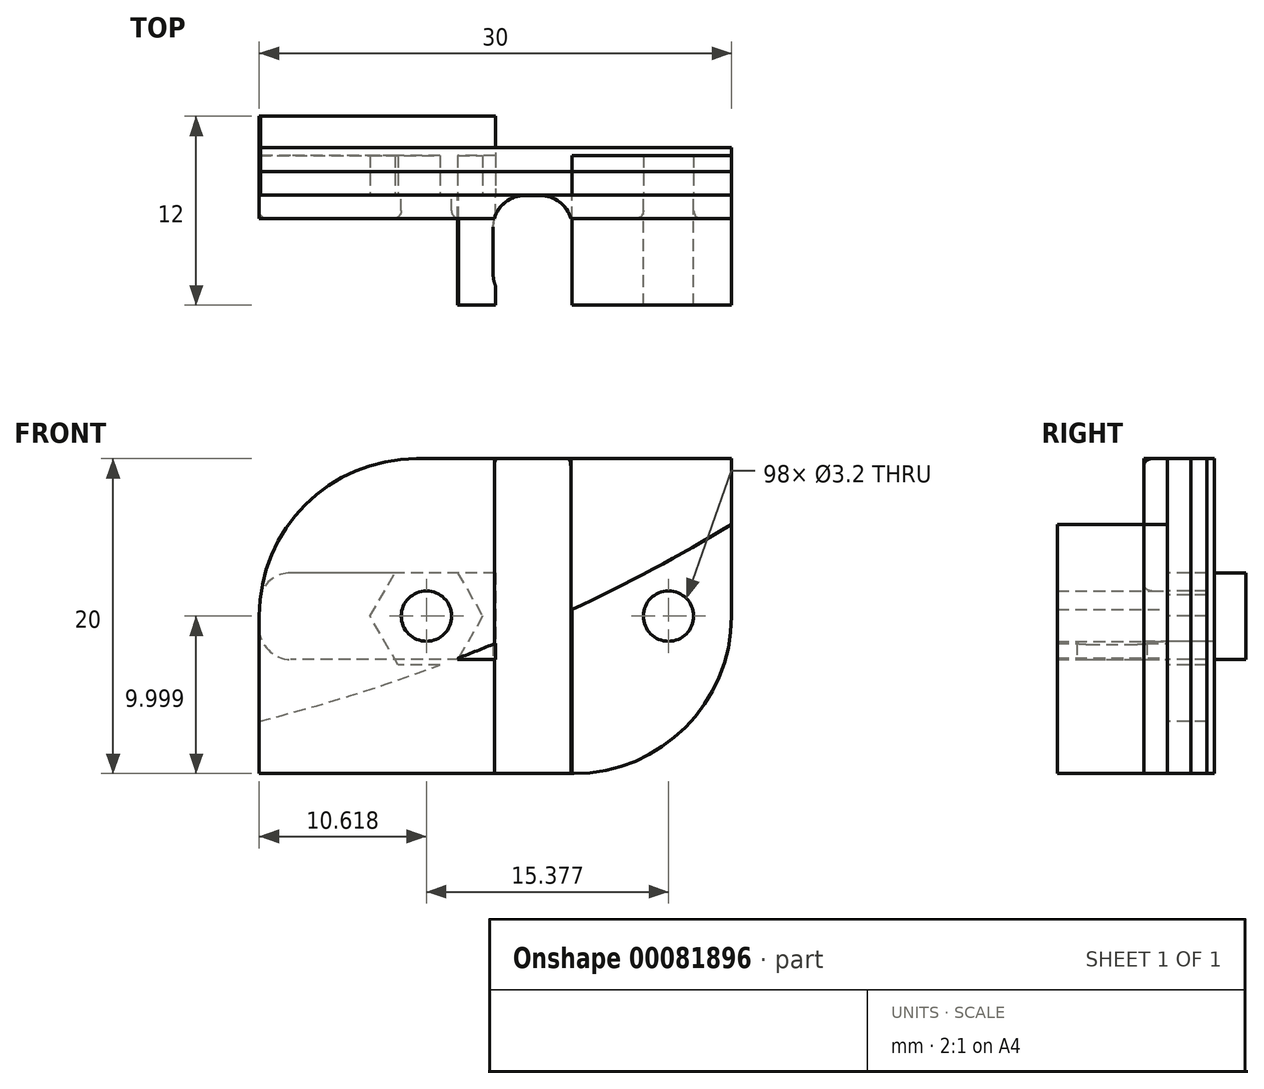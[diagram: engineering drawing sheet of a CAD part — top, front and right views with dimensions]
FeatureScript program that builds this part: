
annotation { "Feature Type Name" : "Feature", "Feature Type Description" : "" }
export const myFeature = defineFeature(function(context is Context, id is Id, definition is map)
    precondition{}
    {
        {
            var Q0;
            Q0=qCreatedBy(makeId("Front.planeOp"),FACE);
            var sketch = newSketch(context, id + "F0", { "sketchPlane" : qUnion([Q0])});
            skLineSegment(sketch, "E0", {"start": v(-99.36, 18.95) * mm, "end": v(51.56, 18.95) * mm, "construction": true});
            skCircle(sketch, "E1", {"center": v(-82.01, 118.95) * mm, "radius": 110 * mm});
            skLineSegment(sketch, "E2.bottom", {"start": v(-45.16, 28.95) * mm, "end": v(-25.16, 28.95) * mm});
            skLineSegment(sketch, "E2.top", {"start": v(-55.16, 8.95) * mm, "end": v(-35.16, 8.95) * mm});
            skLineSegment(sketch, "E2.left", {"start": v(-55.16, 18.95) * mm, "end": v(-55.16, 8.95) * mm});
            skLineSegment(sketch, "E2.right", {"start": v(-25.16, 28.95) * mm, "end": v(-25.16, 18.95) * mm});
            skCircle(sketch, "E3", {"center": v(-29.16, 18.95) * mm, "radius": 1.6 * mm});
            skCircle(sketch, "E4", {"center": v(-44.54, 18.95) * mm, "radius": 5 * mm, "construction": true});
            skPoint(sketch, "E5.visualSharp", {"position": v(-55.16, 28.95) * mm});
            skArc(sketch, "E5.filletArc", {"start": v(-45.16, 28.95) * mm, "mid": v(-52.24, 26.02) * mm, "end": v(-55.16, 18.95) * mm});
            skPoint(sketch, "E6.visualSharp", {"position": v(-25.16, 8.95) * mm});
            skArc(sketch, "E6.filletArc", {"start": v(-35.16, 8.95) * mm, "mid": v(-28.1, 11.88) * mm, "end": v(-25.16, 18.95) * mm});
            skLineSegment(sketch, "E7.bottom", {"start": v(-40.16, 21.7) * mm, "end": v(-53.16, 21.7) * mm});
            skLineSegment(sketch, "E7.top", {"start": v(-40.16, 16.2) * mm, "end": v(-53.16, 16.2) * mm});
            skLineSegment(sketch, "E7.left", {"start": v(-40.16, 21.7) * mm, "end": v(-40.16, 16.2) * mm});
            skLineSegment(sketch, "E7.right", {"start": v(-55.16, 19.7) * mm, "end": v(-55.16, 18.2) * mm});
            skPoint(sketch, "E7.middle", {"position": v(-47.66, 18.95) * mm});
            skCircle(sketch, "E8", {"center": v(-44.54, 18.95) * mm, "radius": 1.6 * mm});
            skLineSegment(sketch, "E9.bottom", {"start": v(-25.16, 28.95) * mm, "end": v(-35.3, 28.95) * mm});
            skLineSegment(sketch, "E9.top", {"start": v(-35.16, 8.95) * mm, "end": v(-35.3, 8.95) * mm});
            skLineSegment(sketch, "E9.right", {"start": v(-35.3, 28.95) * mm, "end": v(-35.3, 8.95) * mm});
            skPoint(sketch, "E10.visualSharp", {"position": v(-55.16, 21.7) * mm});
            skArc(sketch, "E10.filletArc", {"start": v(-53.16, 21.7) * mm, "mid": v(-54.58, 21.11) * mm, "end": v(-55.16, 19.7) * mm});
            skPoint(sketch, "E11.visualSharp", {"position": v(-55.16, 16.2) * mm});
            skArc(sketch, "E11.filletArc", {"start": v(-55.16, 18.2) * mm, "mid": v(-54.58, 16.78) * mm, "end": v(-53.16, 16.2) * mm});
            skCircle(sketch, "E12.cCircle", {"center": v(-44.54, 18.95) * mm, "radius": 3.1 * mm, "construction": true});
            skLineSegment(sketch, "E12.0", {"start": v(-42.75, 22.05) * mm, "end": v(-40.96, 18.95) * mm});
            skLineSegment(sketch, "E12.1", {"start": v(-40.96, 18.95) * mm, "end": v(-42.75, 15.85) * mm});
            skLineSegment(sketch, "E12.2", {"start": v(-42.75, 15.85) * mm, "end": v(-46.33, 15.85) * mm});
            skLineSegment(sketch, "E12.3", {"start": v(-46.33, 15.85) * mm, "end": v(-48.12, 18.95) * mm});
            skLineSegment(sketch, "E12.4", {"start": v(-48.12, 18.95) * mm, "end": v(-46.33, 22.05) * mm});
            skLineSegment(sketch, "E12.5", {"start": v(-46.33, 22.05) * mm, "end": v(-42.75, 22.05) * mm});
            skPoint(sketch, "E12.0.midPoint", {"position": v(-41.86, 20.5) * mm});
            skSolve(sketch);
        }
        {
            var Q0;
            Q0=makeQuery(id+"F0.imprint","IMPRINT",FACE,{"disambiguationData":[TD([[makeQuery(id+"F0.imprint","IMPRINT",EDGE,{"derivedFrom":sQuery(id+"F0.wireOp",EDGE,"E3")}),-1.0]])]});
            var Q1;
            {var subQ5=sQuery(id+"F0.wireOp",EDGE,"E9.bottom");Q1=makeQuery(id+"F0.imprint","IMPRINT",FACE,{"disambiguationData":[TD([[makeQuery(id+"F0.imprint","IMPRINT",EDGE,{"derivedFrom":subQ5}),1.0]])]});}
            var Q2;
            {var subQ12=sQuery(id+"F0.wireOp",EDGE,"E2.bottom");Q2=makeQuery(id+"F0.imprint","IMPRINT",FACE,{"disambiguationData":[TD([[makeQuery(id+"F0.imprint","IMPRINT",EDGE,{"derivedFrom":subQ12}),-1.0]])]});}
            var Q3;
            {var subQ1=sQuery(id+"F0.wireOp",EDGE,"E2.top");Q3=makeQuery(id+"F0.imprint","IMPRINT",FACE,{"disambiguationData":[TD([[makeQuery(id+"F0.imprint","IMPRINT",EDGE,{"derivedFrom":subQ1}),1.0]])]});}
            var Q4;
            {var subQ3=sQuery(id+"F0.wireOp",EDGE,"E7.bottom");var subQ5=sQuery(id+"F0.wireOp",EDGE,"E4");var subQ7=makeQuery(id+"F0.imprint","INTERSECT",VERTEX,{"disambiguationData":[OD(0.0)],"derivedFrom":[subQ5,subQ3]});Q4=makeQuery(id+"F0.imprint","IMPRINT",FACE,{"disambiguationData":[TD([[makeQuery(id+"F0.imprint","IMPRINT",EDGE,{"disambiguationData":[TD([[subQ7,-1.0]])],"derivedFrom":subQ5}),1.0]])]});}
            var Q5;
            {var subQ12=sQuery(id+"F0.wireOp",EDGE,"8888e60d-31c4-49a8-b3cd-6678c98749ca.5");Q5=makeQuery(id+"F0.imprint","IMPRINT",FACE,{"disambiguationData":[TD([[makeQuery(id+"F0.imprint","IMPRINT",EDGE,{"derivedFrom":subQ12}),1.0]])]});}
            var Q6;
            {var subQ0=sQuery(id+"F0.wireOp",EDGE,"E7.left");var subQ1=sQuery(id+"F0.wireOp",EDGE,"E1");var subQ2=makeQuery(id+"F0.imprint","INTERSECT",VERTEX,{"derivedFrom":[subQ1,subQ0]});Q6=makeQuery(id+"F0.imprint","IMPRINT",FACE,{"disambiguationData":[TD([[makeQuery(id+"F0.imprint","IMPRINT",EDGE,{"disambiguationData":[TD([[subQ2,-1.0]])],"derivedFrom":subQ1}),1.0]])]});}
            var Q7;
            {var subQ0=sQuery(id+"F0.wireOp",EDGE,"E4");var subQ1=sQuery(id+"F0.wireOp",EDGE,"E1");var subQ2=makeQuery(id+"F0.imprint","INTERSECT",VERTEX,{"disambiguationData":[OD(0.0)],"derivedFrom":[subQ1,subQ0]});Q7=makeQuery(id+"F0.imprint","IMPRINT",FACE,{"disambiguationData":[TD([[makeQuery(id+"F0.imprint","IMPRINT",EDGE,{"disambiguationData":[TD([[subQ2,-1.0]])],"derivedFrom":subQ1}),-1.0]])]});}
            var Q8;
            {var subQ0=sQuery(id+"F0.wireOp",EDGE,"E7.top");var subQ1=sQuery(id+"F0.wireOp",EDGE,"E1");var subQ2=makeQuery(id+"F0.imprint","INTERSECT",VERTEX,{"derivedFrom":[subQ1,subQ0]});Q8=makeQuery(id+"F0.imprint","IMPRINT",FACE,{"disambiguationData":[TD([[makeQuery(id+"F0.imprint","IMPRINT",EDGE,{"disambiguationData":[TD([[subQ2,-1.0]])],"derivedFrom":subQ1}),-1.0]])]});}
            var Q9;
            {var subQ1=sQuery(id+"F0.wireOp",EDGE,"E4");var subQ5=sQuery(id+"F0.wireOp",EDGE,"E1");var subQ9=makeQuery(id+"F0.imprint","INTERSECT",VERTEX,{"disambiguationData":[OD(0.0)],"derivedFrom":[subQ5,subQ1]});Q9=makeQuery(id+"F0.imprint","IMPRINT",FACE,{"disambiguationData":[TD([[makeQuery(id+"F0.imprint","IMPRINT",EDGE,{"disambiguationData":[TD([[subQ9,-1.0]])],"derivedFrom":subQ5}),1.0]])]});}
            var Q10;
            Q10=makeQuery(id+"F0.imprint","IMPRINT",FACE,{"disambiguationData":[TD([[makeQuery(id+"F0.imprint","IMPRINT",EDGE,{"derivedFrom":sQuery(id+"F0.wireOp",EDGE,"E8")}),-1.0]])]});
            var Q11;
            {var subQ0=sQuery(id+"F0.wireOp",EDGE,"8888e60d-31c4-49a8-b3cd-6678c98749ca.4");var subQ1=sQuery(id+"F0.wireOp",EDGE,"E7.bottom");var subQ2=makeQuery(id+"F0.imprint","INTERSECT",VERTEX,{"derivedFrom":[subQ1,subQ0]});Q11=makeQuery(id+"F0.imprint","IMPRINT",FACE,{"disambiguationData":[TD([[makeQuery(id+"F0.imprint","IMPRINT",EDGE,{"disambiguationData":[TD([[subQ2,-1.0]])],"derivedFrom":subQ1}),-1.0]])]});}
            var Q12;
            {var subQ5=sQuery(id+"F0.wireOp",EDGE,"8888e60d-31c4-49a8-b3cd-6678c98749ca.2");Q12=makeQuery(id+"F0.imprint","IMPRINT",FACE,{"disambiguationData":[TD([[makeQuery(id+"F0.imprint","IMPRINT",EDGE,{"derivedFrom":subQ5}),1.0]])]});}
            var Q13;
            {var subQ0=sQuery(id+"F0.wireOp",EDGE,"E11.filletArc");Q13=makeQuery(id+"F0.imprint","IMPRINT",FACE,{"disambiguationData":[TD([[makeQuery(id+"F0.imprint","IMPRINT",EDGE,{"derivedFrom":subQ0}),1.0]])]});}
            var Q14;
            {var subQ5=sQuery(id+"F0.wireOp",EDGE,"E11.filletArc");Q14=makeQuery(id+"F0.imprint","IMPRINT",FACE,{"disambiguationData":[TD([[makeQuery(id+"F0.imprint","IMPRINT",EDGE,{"derivedFrom":subQ5}),-1.0]])]});}
            var Q15;
            {var subQ0=sQuery(id+"F0.wireOp",EDGE,"8888e60d-31c4-49a8-b3cd-6678c98749ca.0");var subQ1=sQuery(id+"F0.wireOp",EDGE,"E7.top");var subQ2=makeQuery(id+"F0.imprint","INTERSECT",VERTEX,{"derivedFrom":[subQ1,subQ0]});Q15=makeQuery(id+"F0.imprint","IMPRINT",FACE,{"disambiguationData":[TD([[makeQuery(id+"F0.imprint","IMPRINT",EDGE,{"disambiguationData":[TD([[subQ2,-1.0]])],"derivedFrom":subQ1}),1.0]])]});}
            var Q16;
            {var subQ0=sQuery(id+"F0.wireOp",EDGE,"E7.left");var subQ1=sQuery(id+"F0.wireOp",EDGE,"E1");var subQ2=makeQuery(id+"F0.imprint","INTERSECT",VERTEX,{"derivedFrom":[subQ1,subQ0]});Q16=makeQuery(id+"F0.imprint","IMPRINT",FACE,{"disambiguationData":[TD([[makeQuery(id+"F0.imprint","IMPRINT",EDGE,{"disambiguationData":[TD([[subQ2,-1.0]])],"derivedFrom":subQ1}),-1.0]])]});}
            var Q17;
            {var subQ0=sQuery(id+"F0.wireOp",EDGE,"E7.top");var subQ1=sQuery(id+"F0.wireOp",EDGE,"E4");var subQ2=makeQuery(id+"F0.imprint","INTERSECT",VERTEX,{"disambiguationData":[OD(1.0)],"derivedFrom":[subQ1,subQ0]});Q17=makeQuery(id+"F0.imprint","IMPRINT",FACE,{"disambiguationData":[TD([[makeQuery(id+"F0.imprint","IMPRINT",EDGE,{"disambiguationData":[TD([[subQ2,-1.0]])],"derivedFrom":subQ1}),-1.0]])]});}
            var Q18;
            {var subQ0=sQuery(id+"F0.wireOp",EDGE,"E7.bottom");var subQ1=sQuery(id+"F0.wireOp",EDGE,"E4");var subQ2=makeQuery(id+"F0.imprint","INTERSECT",VERTEX,{"disambiguationData":[OD(0.0)],"derivedFrom":[subQ1,subQ0]});Q18=makeQuery(id+"F0.imprint","IMPRINT",FACE,{"disambiguationData":[TD([[makeQuery(id+"F0.imprint","IMPRINT",EDGE,{"disambiguationData":[TD([[subQ2,1.0]])],"derivedFrom":subQ1}),-1.0]])]});}
            var Q19;
            {var subQ5=sQuery(id+"F0.wireOp",EDGE,"E12.5");Q19=makeQuery(id+"F0.imprint","IMPRINT",FACE,{"disambiguationData":[TD([[makeQuery(id+"F0.imprint","IMPRINT",EDGE,{"derivedFrom":subQ5}),-1.0]])]});}
            var Q20;
            {var subQ0=sQuery(id+"F0.wireOp",EDGE,"E12.1");var subQ5=sQuery(id+"F0.wireOp",EDGE,"E1");var subQ6=makeQuery(id+"F0.imprint","INTERSECT",VERTEX,{"derivedFrom":[subQ5,subQ0]});Q20=makeQuery(id+"F0.imprint","IMPRINT",FACE,{"disambiguationData":[TD([[makeQuery(id+"F0.imprint","IMPRINT",EDGE,{"disambiguationData":[TD([[subQ6,-1.0]])],"derivedFrom":subQ5}),1.0]])]});}
            var Q21;
            {var subQ0=sQuery(id+"F0.wireOp",EDGE,"E12.1");var subQ1=sQuery(id+"F0.wireOp",EDGE,"E1");var subQ2=makeQuery(id+"F0.imprint","INTERSECT",VERTEX,{"derivedFrom":[subQ1,subQ0]});Q21=makeQuery(id+"F0.imprint","IMPRINT",FACE,{"disambiguationData":[TD([[makeQuery(id+"F0.imprint","IMPRINT",EDGE,{"disambiguationData":[TD([[subQ2,-1.0]])],"derivedFrom":subQ1}),-1.0]])]});}
            extrude(context, id + "F1", {"entities" : qUnion([Q0, Q1, Q2, Q3, Q4, Q5, Q6, Q7, Q8, Q9, Q10, Q11, Q12, Q13, Q14, Q15, Q16, Q17, Q18, Q19, Q20, Q21]), "depth" : 1.5 * mm});
        }
        {
            var Q0;
            {var subQ5=sQuery(id+"F0.wireOp",EDGE,"E9.bottom");Q0=makeQuery(id+"F0.imprint","IMPRINT",FACE,{"disambiguationData":[TD([[makeQuery(id+"F0.imprint","IMPRINT",EDGE,{"derivedFrom":subQ5}),1.0]])]});}
            var Q1;
            Q1=makeQuery(id+"F0.imprint","IMPRINT",FACE,{"disambiguationData":[TD([[makeQuery(id+"F0.imprint","IMPRINT",EDGE,{"derivedFrom":sQuery(id+"F0.wireOp",EDGE,"E3")}),-1.0]])]});
            var Q2;
            {var subQ1=sQuery(id+"F0.wireOp",EDGE,"E2.top");Q2=makeQuery(id+"F0.imprint","IMPRINT",FACE,{"disambiguationData":[TD([[makeQuery(id+"F0.imprint","IMPRINT",EDGE,{"derivedFrom":subQ1}),1.0]])]});}
            var Q3;
            {var subQ10=sQuery(id+"F0.wireOp",EDGE,"E2.bottom");Q3=makeQuery(id+"F0.imprint","IMPRINT",FACE,{"disambiguationData":[TD([[makeQuery(id+"F0.imprint","IMPRINT",EDGE,{"derivedFrom":subQ10}),-1.0]])]});}
            var Q4;
            {var subQ0=sQuery(id+"F0.wireOp",EDGE,"E11.filletArc");Q4=makeQuery(id+"F0.imprint","IMPRINT",FACE,{"disambiguationData":[TD([[makeQuery(id+"F0.imprint","IMPRINT",EDGE,{"derivedFrom":subQ0}),-1.0]])]});}
            var Q5;
            {var subQ9=sQuery(id+"F0.wireOp",EDGE,"E11.filletArc");Q5=makeQuery(id+"F0.imprint","IMPRINT",FACE,{"disambiguationData":[TD([[makeQuery(id+"F0.imprint","IMPRINT",EDGE,{"derivedFrom":subQ9}),1.0]])]});}
            var Q6;
            {var subQ0=sQuery(id+"F0.wireOp",EDGE,"E7.bottom");var subQ1=sQuery(id+"F0.wireOp",EDGE,"E4");var subQ2=makeQuery(id+"F0.imprint","INTERSECT",VERTEX,{"disambiguationData":[OD(0.0)],"derivedFrom":[subQ1,subQ0]});Q6=makeQuery(id+"F0.imprint","IMPRINT",FACE,{"disambiguationData":[TD([[makeQuery(id+"F0.imprint","IMPRINT",EDGE,{"disambiguationData":[TD([[subQ2,1.0]])],"derivedFrom":subQ1}),-1.0]])]});}
            var Q7;
            {var subQ0=sQuery(id+"F0.wireOp",EDGE,"E7.top");var subQ1=sQuery(id+"F0.wireOp",EDGE,"E4");var subQ2=makeQuery(id+"F0.imprint","INTERSECT",VERTEX,{"disambiguationData":[OD(1.0)],"derivedFrom":[subQ1,subQ0]});Q7=makeQuery(id+"F0.imprint","IMPRINT",FACE,{"disambiguationData":[TD([[makeQuery(id+"F0.imprint","IMPRINT",EDGE,{"disambiguationData":[TD([[subQ2,-1.0]])],"derivedFrom":subQ1}),-1.0]])]});}
            var Q8;
            {var subQ0=sQuery(id+"F0.wireOp",EDGE,"E12.1");var subQ5=sQuery(id+"F0.wireOp",EDGE,"E1");var subQ6=makeQuery(id+"F0.imprint","INTERSECT",VERTEX,{"derivedFrom":[subQ5,subQ0]});Q8=makeQuery(id+"F0.imprint","IMPRINT",FACE,{"disambiguationData":[TD([[makeQuery(id+"F0.imprint","IMPRINT",EDGE,{"disambiguationData":[TD([[subQ6,-1.0]])],"derivedFrom":subQ5}),1.0]])]});}
            var Q9;
            {var subQ0=sQuery(id+"F0.wireOp",EDGE,"E12.1");var subQ1=sQuery(id+"F0.wireOp",EDGE,"E1");var subQ2=makeQuery(id+"F0.imprint","INTERSECT",VERTEX,{"derivedFrom":[subQ1,subQ0]});Q9=makeQuery(id+"F0.imprint","IMPRINT",FACE,{"disambiguationData":[TD([[makeQuery(id+"F0.imprint","IMPRINT",EDGE,{"disambiguationData":[TD([[subQ2,-1.0]])],"derivedFrom":subQ1}),-1.0]])]});}
            extrude(context, id + "F2", {"entities" : qUnion([Q0, Q1, Q2, Q3, Q4, Q5, Q6, Q7, Q8, Q9]), "oppositeDirection" : true, "depth" : 2.5 * mm});
        }
        {
            var Q0;
            {var subQ1=sQuery(id+"F0.wireOp",EDGE,"E2.top");Q0=makeQuery(id+"F0.imprint","IMPRINT",FACE,{"disambiguationData":[TD([[makeQuery(id+"F0.imprint","IMPRINT",EDGE,{"derivedFrom":subQ1}),1.0]])]});}
            var Q1;
            Q1=makeQuery(id+"F0.imprint","IMPRINT",FACE,{"disambiguationData":[TD([[makeQuery(id+"F0.imprint","IMPRINT",EDGE,{"derivedFrom":sQuery(id+"F0.wireOp",EDGE,"E3")}),-1.0]])]});
            var Q2;
            {var subQ0=sQuery(id+"F0.wireOp",EDGE,"E7.top");var subQ1=sQuery(id+"F0.wireOp",EDGE,"E4");var subQ2=makeQuery(id+"F0.imprint","INTERSECT",VERTEX,{"disambiguationData":[OD(1.0)],"derivedFrom":[subQ1,subQ0]});Q2=makeQuery(id+"F0.imprint","IMPRINT",FACE,{"disambiguationData":[TD([[makeQuery(id+"F0.imprint","IMPRINT",EDGE,{"disambiguationData":[TD([[subQ2,-1.0]])],"derivedFrom":subQ1}),-1.0]])]});}
            var Q3;
            {var subQ0=sQuery(id+"F0.wireOp",EDGE,"E12.1");var subQ1=sQuery(id+"F0.wireOp",EDGE,"E1");var subQ2=makeQuery(id+"F0.imprint","INTERSECT",VERTEX,{"derivedFrom":[subQ1,subQ0]});Q3=makeQuery(id+"F0.imprint","IMPRINT",FACE,{"disambiguationData":[TD([[makeQuery(id+"F0.imprint","IMPRINT",EDGE,{"disambiguationData":[TD([[subQ2,-1.0]])],"derivedFrom":subQ1}),-1.0]])]});}
            extrude(context, id + "F3", {"entities" : qUnion([Q0, Q1, Q2, Q3]), "depth" : 7 * mm});
        }
        {
            var Q0;
            {var subQ9=sQuery(id+"F0.wireOp",EDGE,"E11.filletArc");Q0=makeQuery(id+"F0.imprint","IMPRINT",FACE,{"disambiguationData":[TD([[makeQuery(id+"F0.imprint","IMPRINT",EDGE,{"derivedFrom":subQ9}),1.0]])]});}
            var Q1;
            Q1=makeQuery(id+"F0.imprint","IMPRINT",FACE,{"disambiguationData":[TD([[makeQuery(id+"F0.imprint","IMPRINT",EDGE,{"derivedFrom":sQuery(id+"F0.wireOp",EDGE,"E8")}),-1.0]])]});
            var Q2;
            {var subQ0=sQuery(id+"F0.wireOp",EDGE,"E7.top");var subQ1=sQuery(id+"F0.wireOp",EDGE,"E1");var subQ2=makeQuery(id+"F0.imprint","INTERSECT",VERTEX,{"derivedFrom":[subQ1,subQ0]});Q2=makeQuery(id+"F0.imprint","IMPRINT",FACE,{"disambiguationData":[TD([[makeQuery(id+"F0.imprint","IMPRINT",EDGE,{"disambiguationData":[TD([[subQ2,-1.0]])],"derivedFrom":subQ1}),-1.0]])]});}
            var Q3;
            Q3=makeQuery(id+"F0.imprint","IMPRINT",FACE,{"disambiguationData":[TD([[makeQuery(id+"F0.imprint","IMPRINT",EDGE,{"derivedFrom":sQuery(id+"F0.wireOp",EDGE,"E8")}),1.0]])]});
            var Q4;
            {var subQ0=sQuery(id+"F0.wireOp",EDGE,"E12.1");var subQ5=sQuery(id+"F0.wireOp",EDGE,"E1");var subQ6=makeQuery(id+"F0.imprint","INTERSECT",VERTEX,{"derivedFrom":[subQ5,subQ0]});Q4=makeQuery(id+"F0.imprint","IMPRINT",FACE,{"disambiguationData":[TD([[makeQuery(id+"F0.imprint","IMPRINT",EDGE,{"disambiguationData":[TD([[subQ6,-1.0]])],"derivedFrom":subQ5}),1.0]])]});}
            var Q5;
            {var subQ0=sQuery(id+"F0.wireOp",EDGE,"E12.1");var subQ1=sQuery(id+"F0.wireOp",EDGE,"E1");var subQ2=makeQuery(id+"F0.imprint","INTERSECT",VERTEX,{"derivedFrom":[subQ1,subQ0]});Q5=makeQuery(id+"F0.imprint","IMPRINT",FACE,{"disambiguationData":[TD([[makeQuery(id+"F0.imprint","IMPRINT",EDGE,{"disambiguationData":[TD([[subQ2,-1.0]])],"derivedFrom":subQ1}),-1.0]])]});}
            extrude(context, id + "F4", {"entities" : qUnion([Q0, Q1, Q2, Q3, Q4, Q5]), "oppositeDirection" : true, "depth" : 5 * mm});
        }
        {
            var Q0;
            {var subQ10=sQuery(id+"F0.wireOp",EDGE,"E2.bottom");Q0=makeQuery(id+"F0.imprint","IMPRINT",FACE,{"disambiguationData":[TD([[makeQuery(id+"F0.imprint","IMPRINT",EDGE,{"derivedFrom":subQ10}),-1.0]])]});}
            var Q1;
            {var subQ0=sQuery(id+"F0.wireOp",EDGE,"E7.bottom");var subQ1=sQuery(id+"F0.wireOp",EDGE,"E4");var subQ2=makeQuery(id+"F0.imprint","INTERSECT",VERTEX,{"disambiguationData":[OD(0.0)],"derivedFrom":[subQ1,subQ0]});Q1=makeQuery(id+"F0.imprint","IMPRINT",FACE,{"disambiguationData":[TD([[makeQuery(id+"F0.imprint","IMPRINT",EDGE,{"disambiguationData":[TD([[subQ2,-1.0]])],"derivedFrom":subQ1}),1.0]])]});}
            var Q2;
            {var subQ9=sQuery(id+"F0.wireOp",EDGE,"E11.filletArc");Q2=makeQuery(id+"F0.imprint","IMPRINT",FACE,{"disambiguationData":[TD([[makeQuery(id+"F0.imprint","IMPRINT",EDGE,{"derivedFrom":subQ9}),1.0]])]});}
            var Q3;
            {var subQ0=sQuery(id+"F0.wireOp",EDGE,"E11.filletArc");Q3=makeQuery(id+"F0.imprint","IMPRINT",FACE,{"disambiguationData":[TD([[makeQuery(id+"F0.imprint","IMPRINT",EDGE,{"derivedFrom":subQ0}),-1.0]])]});}
            var Q4;
            {var subQ0=sQuery(id+"F0.wireOp",EDGE,"E4");var subQ1=sQuery(id+"F0.wireOp",EDGE,"E1");var subQ2=makeQuery(id+"F0.imprint","INTERSECT",VERTEX,{"disambiguationData":[OD(0.0)],"derivedFrom":[subQ1,subQ0]});Q4=makeQuery(id+"F0.imprint","IMPRINT",FACE,{"disambiguationData":[TD([[makeQuery(id+"F0.imprint","IMPRINT",EDGE,{"disambiguationData":[TD([[subQ2,-1.0]])],"derivedFrom":subQ1}),1.0]])]});}
            var Q5;
            {var subQ0=sQuery(id+"F0.wireOp",EDGE,"E4");var subQ1=sQuery(id+"F0.wireOp",EDGE,"E1");var subQ2=makeQuery(id+"F0.imprint","INTERSECT",VERTEX,{"disambiguationData":[OD(0.0)],"derivedFrom":[subQ1,subQ0]});Q5=makeQuery(id+"F0.imprint","IMPRINT",FACE,{"disambiguationData":[TD([[makeQuery(id+"F0.imprint","IMPRINT",EDGE,{"disambiguationData":[TD([[subQ2,-1.0]])],"derivedFrom":subQ1}),-1.0]])]});}
            var Q6;
            Q6=makeQuery(id+"F0.imprint","IMPRINT",FACE,{"disambiguationData":[TD([[makeQuery(id+"F0.imprint","IMPRINT",EDGE,{"derivedFrom":sQuery(id+"F0.wireOp",EDGE,"E8")}),-1.0]])]});
            var Q7;
            {var subQ0=sQuery(id+"F0.wireOp",EDGE,"E7.left");var subQ1=sQuery(id+"F0.wireOp",EDGE,"E1");var subQ2=makeQuery(id+"F0.imprint","INTERSECT",VERTEX,{"derivedFrom":[subQ1,subQ0]});Q7=makeQuery(id+"F0.imprint","IMPRINT",FACE,{"disambiguationData":[TD([[makeQuery(id+"F0.imprint","IMPRINT",EDGE,{"disambiguationData":[TD([[subQ2,-1.0]])],"derivedFrom":subQ1}),1.0]])]});}
            var Q8;
            {var subQ0=sQuery(id+"F0.wireOp",EDGE,"E7.top");var subQ1=sQuery(id+"F0.wireOp",EDGE,"E1");var subQ2=makeQuery(id+"F0.imprint","INTERSECT",VERTEX,{"derivedFrom":[subQ1,subQ0]});Q8=makeQuery(id+"F0.imprint","IMPRINT",FACE,{"disambiguationData":[TD([[makeQuery(id+"F0.imprint","IMPRINT",EDGE,{"disambiguationData":[TD([[subQ2,-1.0]])],"derivedFrom":subQ1}),-1.0]])]});}
            var Q9;
            {var subQ1=sQuery(id+"F0.wireOp",EDGE,"E2.top");Q9=makeQuery(id+"F0.imprint","IMPRINT",FACE,{"disambiguationData":[TD([[makeQuery(id+"F0.imprint","IMPRINT",EDGE,{"derivedFrom":subQ1}),1.0]])]});}
            var Q10;
            Q10=makeQuery(id+"F0.imprint","IMPRINT",FACE,{"disambiguationData":[TD([[makeQuery(id+"F0.imprint","IMPRINT",EDGE,{"derivedFrom":sQuery(id+"F0.wireOp",EDGE,"E3")}),-1.0]])]});
            var Q11;
            {var subQ5=sQuery(id+"F0.wireOp",EDGE,"E9.bottom");Q11=makeQuery(id+"F0.imprint","IMPRINT",FACE,{"disambiguationData":[TD([[makeQuery(id+"F0.imprint","IMPRINT",EDGE,{"derivedFrom":subQ5}),1.0]])]});}
            var Q12;
            {var subQ0=sQuery(id+"F0.wireOp",EDGE,"E7.left");var subQ1=sQuery(id+"F0.wireOp",EDGE,"E1");var subQ2=makeQuery(id+"F0.imprint","INTERSECT",VERTEX,{"derivedFrom":[subQ1,subQ0]});Q12=makeQuery(id+"F0.imprint","IMPRINT",FACE,{"disambiguationData":[TD([[makeQuery(id+"F0.imprint","IMPRINT",EDGE,{"disambiguationData":[TD([[subQ2,-1.0]])],"derivedFrom":subQ1}),-1.0]])]});}
            var Q13;
            {var subQ0=sQuery(id+"F0.wireOp",EDGE,"E7.top");var subQ1=sQuery(id+"F0.wireOp",EDGE,"E4");var subQ2=makeQuery(id+"F0.imprint","INTERSECT",VERTEX,{"disambiguationData":[OD(1.0)],"derivedFrom":[subQ1,subQ0]});Q13=makeQuery(id+"F0.imprint","IMPRINT",FACE,{"disambiguationData":[TD([[makeQuery(id+"F0.imprint","IMPRINT",EDGE,{"disambiguationData":[TD([[subQ2,-1.0]])],"derivedFrom":subQ1}),-1.0]])]});}
            var Q14;
            {var subQ0=sQuery(id+"F0.wireOp",EDGE,"E7.bottom");var subQ1=sQuery(id+"F0.wireOp",EDGE,"E4");var subQ2=makeQuery(id+"F0.imprint","INTERSECT",VERTEX,{"disambiguationData":[OD(0.0)],"derivedFrom":[subQ1,subQ0]});Q14=makeQuery(id+"F0.imprint","IMPRINT",FACE,{"disambiguationData":[TD([[makeQuery(id+"F0.imprint","IMPRINT",EDGE,{"disambiguationData":[TD([[subQ2,1.0]])],"derivedFrom":subQ1}),-1.0]])]});}
            var Q15;
            Q15=makeQuery(id+"F1.opExtrude","CAP_FACE",FACE,{"disambiguationData":[OSD([sQuery(id+"F0.wireOp",EDGE,"E2.bottom"),sQuery(id+"F0.wireOp",EDGE,"E2.top"),sQuery(id+"F0.wireOp",EDGE,"E2.left"),sQuery(id+"F0.wireOp",EDGE,"E3"),sQuery(id+"F0.wireOp",EDGE,"E5.filletArc"),sQuery(id+"F0.wireOp",EDGE,"E7.right"),sQuery(id+"F0.wireOp",EDGE,"E8"),sQuery(id+"F0.wireOp",EDGE,"E9.bottom"),sQuery(id+"F0.wireOp",EDGE,"E9.top"),sQuery(id+"F0.wireOp",EDGE,"E2.right"),sQuery(id+"F0.wireOp",EDGE,"E6.filletArc")])],"isStart":false});
            var Q16;
            {var subQ0=sQuery(id+"F0.wireOp",EDGE,"E12.1");var subQ1=sQuery(id+"F0.wireOp",EDGE,"E1");var subQ2=makeQuery(id+"F0.imprint","INTERSECT",VERTEX,{"derivedFrom":[subQ1,subQ0]});Q16=makeQuery(id+"F0.imprint","IMPRINT",FACE,{"disambiguationData":[TD([[makeQuery(id+"F0.imprint","IMPRINT",EDGE,{"disambiguationData":[TD([[subQ2,-1.0]])],"derivedFrom":subQ1}),-1.0]])]});}
            var Q17;
            {var subQ0=sQuery(id+"F0.wireOp",EDGE,"E12.1");var subQ5=sQuery(id+"F0.wireOp",EDGE,"E1");var subQ6=makeQuery(id+"F0.imprint","INTERSECT",VERTEX,{"derivedFrom":[subQ5,subQ0]});Q17=makeQuery(id+"F0.imprint","IMPRINT",FACE,{"disambiguationData":[TD([[makeQuery(id+"F0.imprint","IMPRINT",EDGE,{"disambiguationData":[TD([[subQ6,-1.0]])],"derivedFrom":subQ5}),1.0]])]});}
            var Q18;
            {var subQ5=sQuery(id+"F0.wireOp",EDGE,"E12.5");Q18=makeQuery(id+"F0.imprint","IMPRINT",FACE,{"disambiguationData":[TD([[makeQuery(id+"F0.imprint","IMPRINT",EDGE,{"derivedFrom":subQ5}),-1.0]])]});}
            var Q19;
            Q19=makeQuery(id+"F0.imprint","IMPRINT",FACE,{"disambiguationData":[TD([[makeQuery(id+"F0.imprint","IMPRINT",EDGE,{"derivedFrom":sQuery(id+"F0.wireOp",EDGE,"E8")}),1.0]])]});
            var Q20;
            {var subQ0=sQuery(id+"F0.wireOp",EDGE,"E12.2");var subQ1=sQuery(id+"F0.wireOp",EDGE,"E1");var subQ2=makeQuery(id+"F0.imprint","INTERSECT",VERTEX,{"derivedFrom":[subQ1,subQ0]});Q20=makeQuery(id+"F0.imprint","IMPRINT",FACE,{"disambiguationData":[TD([[makeQuery(id+"F0.imprint","IMPRINT",EDGE,{"disambiguationData":[TD([[subQ2,-1.0]])],"derivedFrom":subQ1}),-1.0]])]});}
            extrude(context, id + "F5", {"entities" : qUnion([Q0, Q1, Q2, Q3, Q4, Q5, Q6, Q7, Q8, Q9, Q10, Q11, Q12, Q13, Q14, Q15, Q16, Q17, Q18, Q19, Q20]), "oppositeDirection" : true, "depth" : 3 * mm});
        }
        {
            var Q0;
            Q0=qCreatedBy(makeId("Top.planeOp"),FACE);
            var sketch = newSketch(context, id + "F6", { "sketchPlane" : qUnion([Q0])});
            skLineSegment(sketch, "E13.bottom", {"start": v(-38.3, -7.04) * mm, "end": v(-37.3, -7.04) * mm});
            skLineSegment(sketch, "E13.top", {"start": v(-38.3, -0.04) * mm, "end": v(-37.3, -0.04) * mm});
            skLineSegment(sketch, "E13.left", {"start": v(-40.3, -5.04) * mm, "end": v(-40.3, -2.04) * mm});
            skLineSegment(sketch, "E13.right", {"start": v(-35.3, -5.04) * mm, "end": v(-35.3, -2.04) * mm});
            skPoint(sketch, "E14.visualSharp", {"position": v(-40.3, -7.04) * mm});
            skArc(sketch, "E14.filletArc", {"start": v(-40.3, -5.04) * mm, "mid": v(-39.71, -6.45) * mm, "end": v(-38.3, -7.04) * mm});
            skPoint(sketch, "E15.visualSharp", {"position": v(-35.3, -7.04) * mm});
            skArc(sketch, "E15.filletArc", {"start": v(-37.3, -7.04) * mm, "mid": v(-35.89, -6.45) * mm, "end": v(-35.3, -5.04) * mm});
            skPoint(sketch, "E16.visualSharp", {"position": v(-35.3, -0.04) * mm});
            skArc(sketch, "E16.filletArc", {"start": v(-35.3, -2.04) * mm, "mid": v(-35.89, -0.62) * mm, "end": v(-37.3, -0.04) * mm});
            skPoint(sketch, "E17.visualSharp", {"position": v(-40.3, -0.04) * mm});
            skArc(sketch, "E17.filletArc", {"start": v(-38.3, -0.04) * mm, "mid": v(-39.71, -0.62) * mm, "end": v(-40.3, -2.04) * mm});
            skSolve(sketch);
        }
        {
            var Q0;
            Q0=makeQuery(id+"F6.imprint","IMPRINT",FACE,{"disambiguationData":[TD([[makeQuery(id+"F6.imprint","IMPRINT",EDGE,{"derivedFrom":sQuery(id+"F6.wireOp",EDGE,"E13.bottom")}),1.0]])]});
            extrude(context, id + "F7", {"entities" : qUnion([Q0]), "operationType" : NewBodyOperationType.REMOVE, "depth" : 35.8 * mm});
        }
        {
            var Q0;
            Q0=makeQuery(id+"F1.opExtrude","CAP_EDGE",EDGE,{"disambiguationData":[OSD([sQuery(id+"F0.wireOp",EDGE,"E2.bottom"),sQuery(id+"F0.wireOp",EDGE,"E9.bottom")])],"isStart":false});
            var Q1;
            Q1=makeQuery(id+"F1.opExtrude","CAP_EDGE",EDGE,{"disambiguationData":[OSD([sQuery(id+"F0.wireOp",EDGE,"E2.right")])],"isStart":false});
            fillet(context, id + "F8", {"entities" : qUnion([Q0, Q1]), "radius" : .5 * mm, "tangentPropagation" : true, "allowEdgeOverflow" : false});
        }
        {
            var Q0;
            Q0=makeQuery(id+"F7.boolean.opBoolean","INTERSECT",EDGE,{"derivedFrom":[makeQuery(id+"F3.opExtrude","SWEPT_FACE",FACE,{"disambiguationData":[OSD([sQuery(id+"F0.wireOp",EDGE,"E2.top"),sQuery(id+"F0.wireOp",EDGE,"E9.top")])]}),makeQuery(id+"F7.opExtrude","SWEPT_FACE",FACE,{"disambiguationData":[OSD([sQuery(id+"F6.wireOp",EDGE,"E13.left")])]})]});
            var Q1;
            Q1=makeQuery(id+"F1.opExtrude","CAP_EDGE",EDGE,{"disambiguationData":[OSD([sQuery(id+"F0.wireOp",EDGE,"E8")])],"isStart":false});
            var Q2;
            Q2=makeQuery(id+"F1.opExtrude","CAP_EDGE",EDGE,{"disambiguationData":[OSD([sQuery(id+"F0.wireOp",EDGE,"E3")])],"isStart":false});
            fillet(context, id + "F9", {"entities" : qUnion([Q0, Q1, Q2]), "radius" : .5 * mm, "tangentPropagation" : true, "allowEdgeOverflow" : false});
        }
    });
